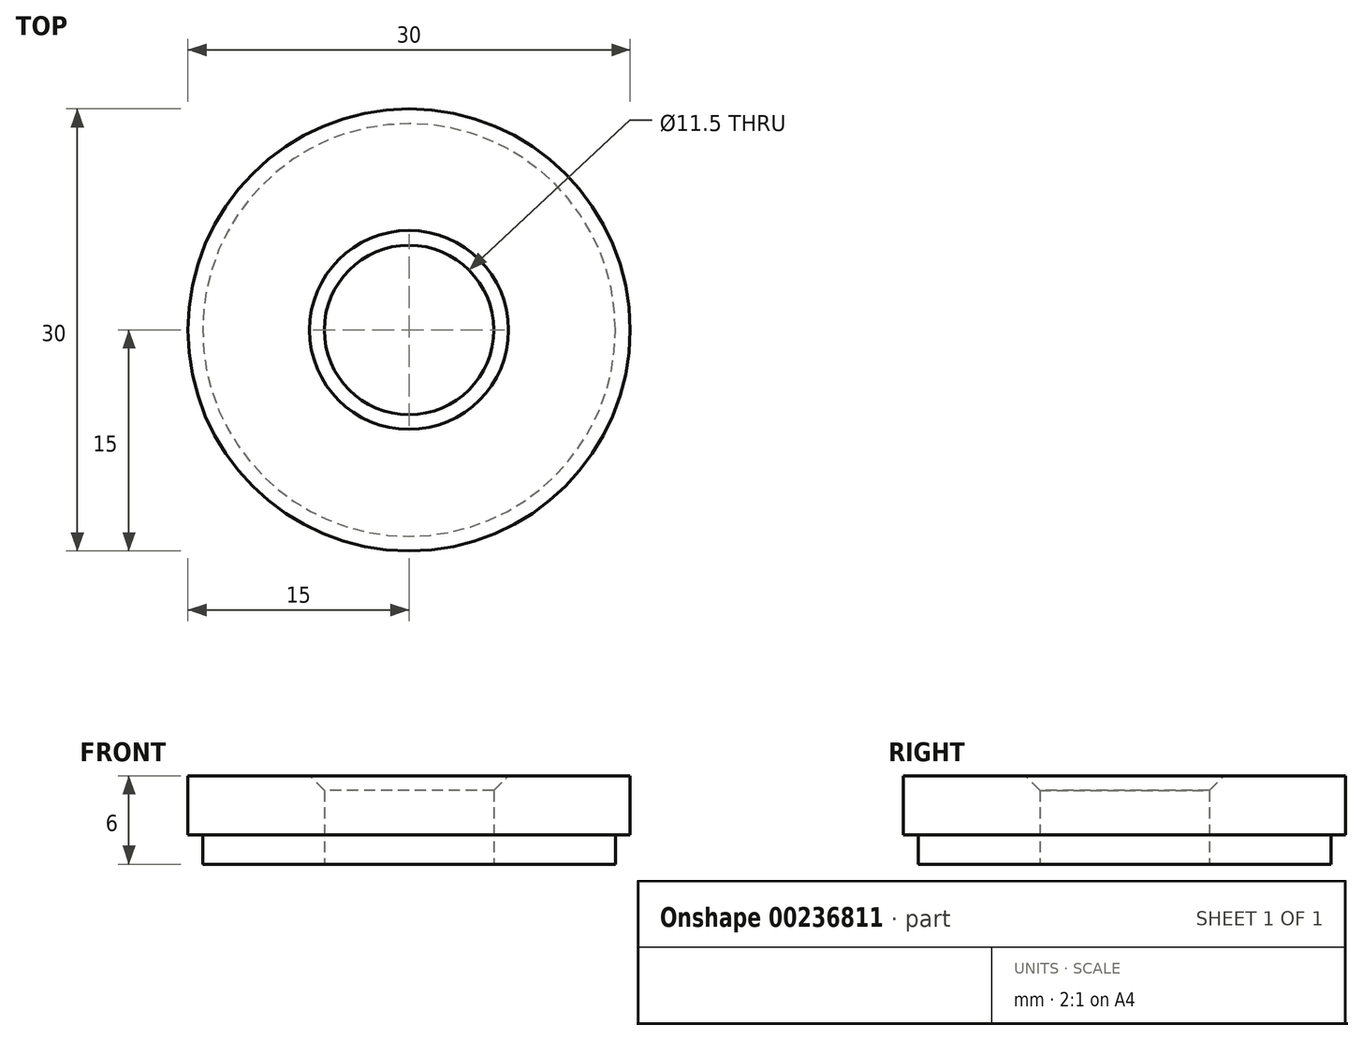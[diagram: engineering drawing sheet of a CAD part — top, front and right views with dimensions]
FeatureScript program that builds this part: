
annotation { "Feature Type Name" : "Feature", "Feature Type Description" : "" }
export const myFeature = defineFeature(function(context is Context, id is Id, definition is map)
    precondition{}
    {
        {
            var Q0;
            Q0=qCreatedBy(makeId("Top.planeOp"),FACE);
            var sketch = newSketch(context, id + "F0", { "sketchPlane" : qUnion([Q0])});
            skCircle(sketch, "E0", {"center": v(0, 0) * mm, "radius": 15 * mm});
            skCircle(sketch, "E1", {"center": v(0, 0) * mm, "radius": 5.75 * mm});
            skSolve(sketch);
        }
        {
            var Q0;
            Q0 = qSketchRegion(id + "F0", true);
            extrude(context, id + "F1", {"entities" : qUnion([Q0]), "depth" : 6 * mm});
        }
        {
            var Q0;
            Q0=makeQuery(id+"F1.opExtrude","CAP_FACE",FACE,{"disambiguationData":[OSD([sQuery(id+"F0.wireOp",EDGE,"E0"),sQuery(id+"F0.wireOp",EDGE,"E1")])],"isStart":true});
            var sketch = newSketch(context, id + "F2", { "sketchPlane" : qUnion([Q0])});
            skCircle(sketch, "E2", {"center": v(0, 0) * mm, "radius": 14 * mm});
            skSolve(sketch);
        }
        {
            var Q0;
            Q0=makeQuery(id+"F2.imprint","IMPRINT",FACE,{"disambiguationData":[TD([[makeQuery(id+"F2.imprint","IMPRINT",EDGE,{"derivedFrom":sQuery(id+"F2.wireOp",EDGE,"E2")}),-1.0]])]});
            extrude(context, id + "F3", {"entities" : qUnion([Q0]), "operationType" : NewBodyOperationType.REMOVE, "oppositeDirection" : true, "depth" : 2 * mm});
        }
        {
            var Q0;
            Q0=makeQuery(id+"F1.opExtrude","CAP_EDGE",EDGE,{"disambiguationData":[OSD([sQuery(id+"F0.wireOp",EDGE,"E1")])],"isStart":false});
            chamfer(context, id + "F4", {"entities" : qUnion([Q0]), "width" : 1 * mm, "tangentPropagation" : true});
        }
    });
